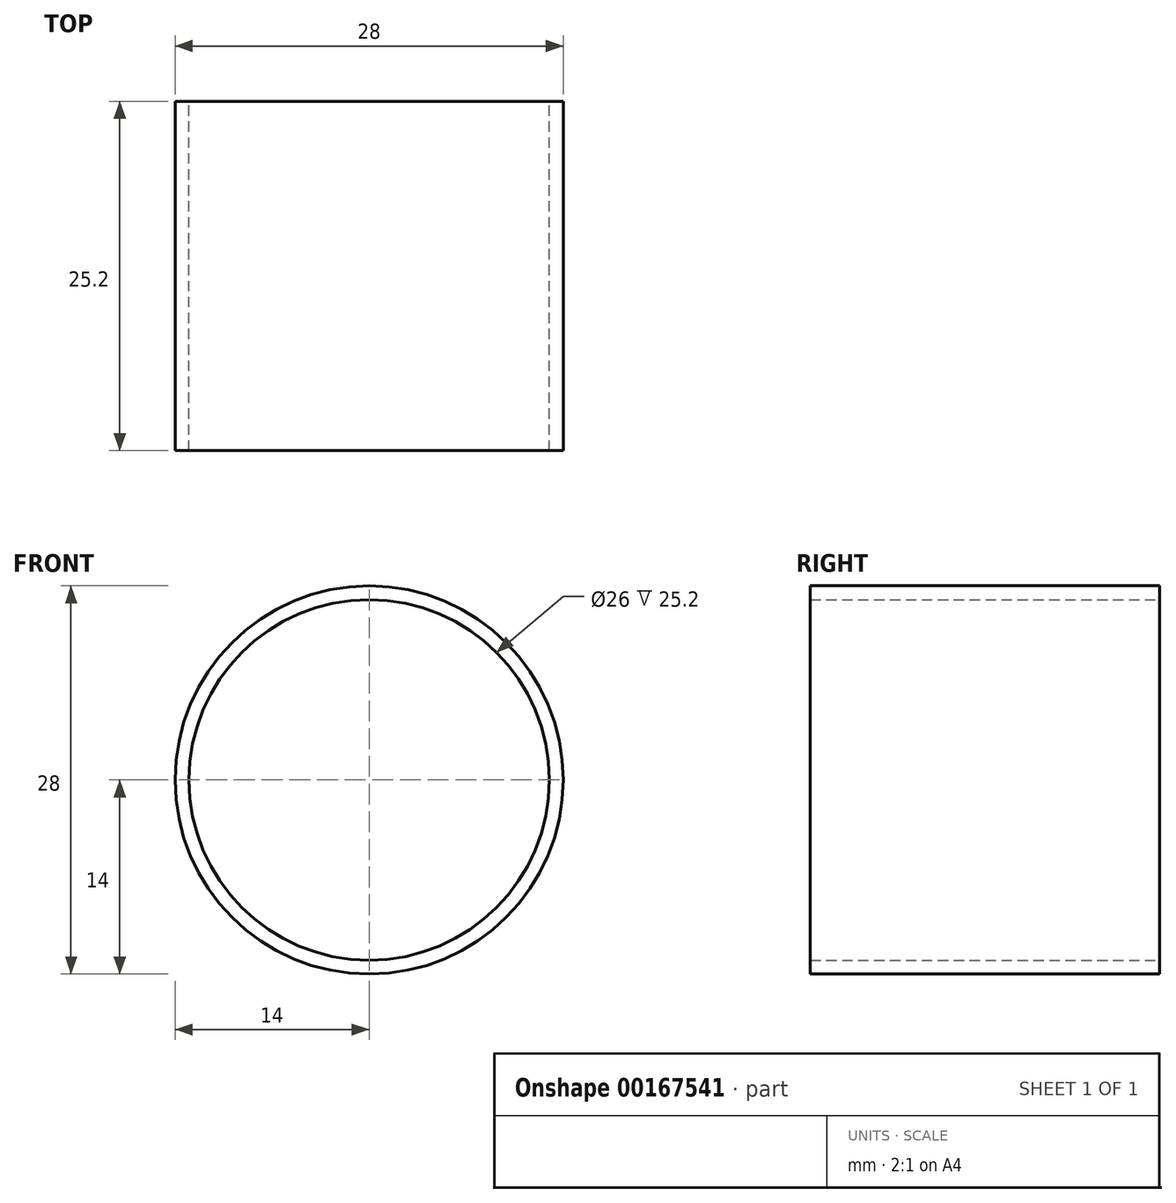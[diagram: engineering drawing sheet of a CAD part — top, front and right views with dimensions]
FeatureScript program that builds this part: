
annotation { "Feature Type Name" : "Feature", "Feature Type Description" : "" }
export const myFeature = defineFeature(function(context is Context, id is Id, definition is map)
    precondition{}
    {
        {
            var Q0;
            Q0=qCreatedBy(makeId("Front.planeOp"),FACE);
            var sketch = newSketch(context, id + "F0", { "sketchPlane" : qUnion([Q0])});
            skCircle(sketch, "E0", {"center": v(0, 0) * mm, "radius": 14 * mm});
            skCircle(sketch, "E1", {"center": v(0, 0) * mm, "radius": 13 * mm});
            skSolve(sketch);
        }
        {
            var Q0;
            Q0=qSketchRegion(id+"F0",true);
            extrude(context, id + "F1", {"entities" : qUnion([Q0]), "depth" : 25.2 * mm, "symmetric" : true});
        }
    });
